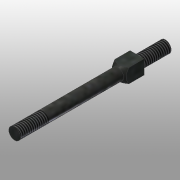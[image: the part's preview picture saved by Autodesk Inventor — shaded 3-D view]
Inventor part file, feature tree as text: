
AUTODESK INVENTOR PART (.ipt)
format: ipt  version: 2016 (Build 200138000, 138)  size: 118,784 bytes
history: native  units: mm
features: sketch x4, extrude x3, thread x2, revolve x1, projected_geometry x1
ambient origin geometry x8: Origin, YZ Plane, XZ Plane, XY Plane, X Axis, Y Axis, Z Axis, Center Point
bodies: Solid1 (feature_tree)
feature tree (11):
  extrude  "Extrusion1"  Depth=3.0mm
  extrude  "Extrusion2"  Depth=2.5mm
  extrude  "Extrusion3"  Depth=2.5mm
  thread  "Thread1"  [1 undecoded]
  thread  "Thread2"  [1 undecoded]
  revolve  "Revolution1"  Angle=45.0deg
  sketch  "Sketch1"  dims[d0=3.0mm d1=3.0mm]
  sketch  "Sketch2"  dims[d2=4.1mm d3=0.0mm d4=2.5mm]
  sketch  "Sketch3"  dims[d5=6.0mm d6=0.0mm d7=2.5mm d8=21.9mm d9=0.0mm d10=6.0mm d11=0.0mm]
  sketch  "Sketch4"  dims[d12=10.0mm d13=0.0mm d15=45.0deg d16=90.0deg]
  projected_geometry  "Project Cut Edges1"
note: 2 required parameter values undecoded (feature->parameter linkage not recoverable at this tier; creation-order binding heuristic only, values carry confidence <= 0.55)
